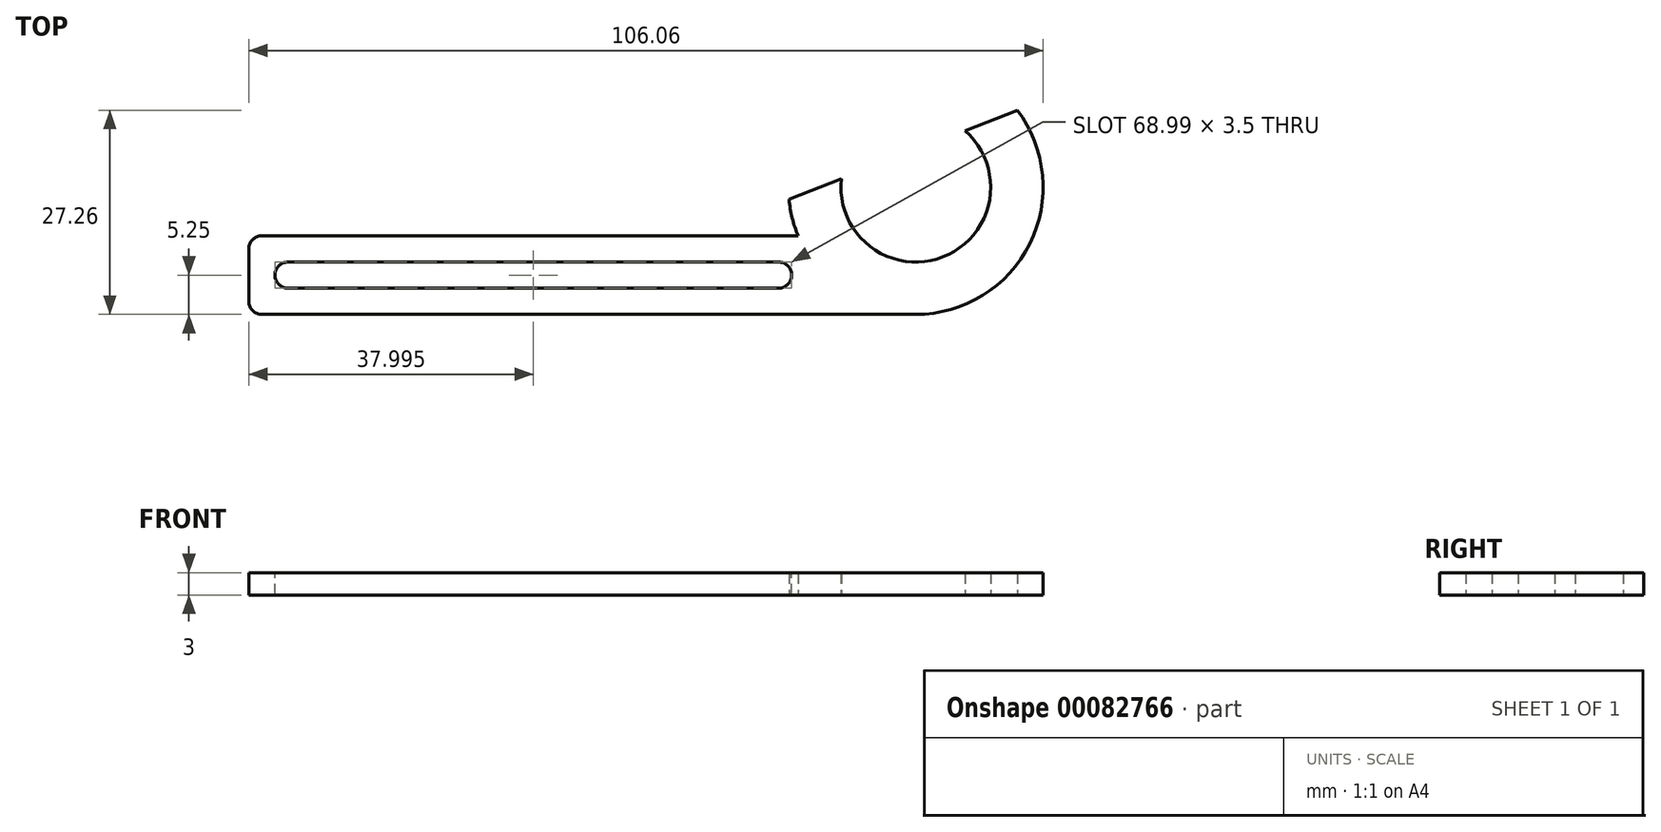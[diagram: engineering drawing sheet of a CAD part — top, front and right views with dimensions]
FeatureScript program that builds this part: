
annotation { "Feature Type Name" : "Feature", "Feature Type Description" : "" }
export const myFeature = defineFeature(function(context is Context, id is Id, definition is map)
    precondition{}
    {
        {
            assignVariable(context, id + "F0", {"name" : "BoltDiameter", "anyValue" : 3.5});
        }
        {
            var Q0;
            Q0=qCreatedBy(makeId("Top.planeOp"),FACE);
            var sketch = newSketch(context, id + "F1", { "sketchPlane" : qUnion([Q0])});
            skLineSegment(sketch, "E0", {"start": v(0, 0) * mm, "end": v(89.06, 0) * mm});
            skLineSegment(sketch, "E1", {"start": v(0, 0) * mm, "end": v(0, 10.5) * mm});
            skLineSegment(sketch, "E2", {"start": v(0, 10.5) * mm, "end": v(73.35, 10.5) * mm});
            skLineSegment(sketch, "E3", {"start": v(3.5, 7) * mm, "end": v(3.5, 3.5) * mm});
            skLineSegment(sketch, "E4", {"start": v(3.5, 3.5) * mm, "end": v(72.5, 3.5) * mm});
            skLineSegment(sketch, "E5", {"start": v(72.5, 3.5) * mm, "end": v(72.5, 7) * mm});
            skLineSegment(sketch, "E6", {"start": v(72.5, 7) * mm, "end": v(3.5, 7) * mm});
            skLineSegment(sketch, "E7", {"start": v(3.5, 5.25) * mm, "end": v(0, 5.25) * mm, "construction": true});
            skCircle(sketch, "E8", {"center": v(89.06, 17) * mm, "radius": 10 * mm});
            skCircle(sketch, "E9", {"center": v(89.06, 17) * mm, "radius": 17 * mm});
            skLineSegment(sketch, "E10", {"start": v(59.65, 10.5) * mm, "end": v(102.6, 27.26) * mm});
            skSolve(sketch);
        }
        {
            var Q0;
            Q0=makeQuery(id+"F1.imprint","IMPRINT",FACE,{"disambiguationData":[TD([[makeQuery(id+"F1.imprint","IMPRINT",EDGE,{"derivedFrom":sQuery(id+"F1.wireOp",EDGE,"E0")}),1.0]])]});
            var Q1;
            {var subQ2=sQuery(id+"F1.wireOp",EDGE,"E10");var subQ4=sQuery(id+"F1.wireOp",EDGE,"E8");var subQ8=makeQuery(id+"F1.imprint","INTERSECT",VERTEX,{"disambiguationData":[OD(0.0)],"derivedFrom":[subQ4,subQ2]});Q1=makeQuery(id+"F1.imprint","IMPRINT",FACE,{"disambiguationData":[TD([[makeQuery(id+"F1.imprint","IMPRINT",EDGE,{"disambiguationData":[TD([[subQ8,-1.0]])],"derivedFrom":subQ4}),-1.0]])]});}
            extrude(context, id + "F2", {"entities" : qUnion([Q0, Q1]), "depth" : 3 * mm});
        }
        {
            var Q0;
            Q0=makeQuery(id+"F2.opExtrude","SWEPT_EDGE",EDGE,{"disambiguationData":[OSD([sQuery(id+"F1.wireOp",EDGE,"E3"),sQuery(id+"F1.wireOp",EDGE,"E6")])]});
            var Q1;
            Q1=makeQuery(id+"F2.opExtrude","SWEPT_EDGE",EDGE,{"disambiguationData":[OSD([sQuery(id+"F1.wireOp",EDGE,"E3"),sQuery(id+"F1.wireOp",EDGE,"E4")])]});
            var Q2;
            Q2=makeQuery(id+"F2.opExtrude","SWEPT_EDGE",EDGE,{"disambiguationData":[OSD([sQuery(id+"F1.wireOp",EDGE,"E1"),sQuery(id+"F1.wireOp",EDGE,"E2")])]});
            var Q3;
            Q3=makeQuery(id+"F2.opExtrude","SWEPT_EDGE",EDGE,{"disambiguationData":[OSD([sQuery(id+"F1.wireOp",EDGE,"E0"),sQuery(id+"F1.wireOp",EDGE,"E1")])]});
            var Q4;
            Q4=makeQuery(id+"F2.opExtrude","SWEPT_EDGE",EDGE,{"disambiguationData":[OSD([sQuery(id+"F1.wireOp",EDGE,"E5"),sQuery(id+"F1.wireOp",EDGE,"E6")])]});
            var Q5;
            Q5=makeQuery(id+"F2.opExtrude","SWEPT_EDGE",EDGE,{"disambiguationData":[OSD([sQuery(id+"F1.wireOp",EDGE,"E4"),sQuery(id+"F1.wireOp",EDGE,"E5")])]});
            fillet(context, id + "F3", {"entities" : qUnion([Q0, Q1, Q2, Q3, Q4, Q5]), "radius" : (getVariable(context, 'BoltDiameter') / 2) * mm, "tangentPropagation" : true, "allowEdgeOverflow" : false});
        }
    });
